# Revit family: HydroTap_Mixer_Zip_Arc
name_source: partatom
category: Plumbing Fixtures
revit_build: Autodesk Revit 2018 (Build: 20190510_1515(x64)
units: mm (PartAtom-declared; Revit-internal decimal feet)

## family parameters
Always vertical = No
Cut with Voids When Loaded = Yes
OmniClass Number = 23.45.55.17
OmniClass Title = Mixing Faucets
Part Type = Normal
Room Calculation Point = No
Round Connector Dimension = Use Diameter
Shared = No
Work Plane-Based = Yes

## types (9) — shared parameters
CW Connection = Yes
HW Connection = Yes
IfcExportAs = IfcValve
IfcExportType = FAUCET
Manufacturer = Zip Australia
ManufacturerOverallDepth = 200 mm
ManufacturerOverallHeight = 353 mm
ManufacturerOverallWidth = 90 mm
ManufacturerURLProductSpecific = https://www.zipwater.com
ModifiedIssue = 20210225 $
URL = https://www.zipwater.com
Uniclass2015Code = Pr_40_20_87_55
Uniclass2015Title = Mixer taps
Uniclass2015Version = Products v1.17
Vent Connection = No
Waste Connection = No
zero-valued in all types: Default Elevation

## per-type parameters (varying)
| type | FixtureMaterial | ManufacturerSpecCode | Model | Type Comments |
| Matte White (Z14) | Metal_MatteWhite_Zip | Z14 | Z14 | Matte White Finish |
| Brushed Stainless Steel (Z13) | Metal_BrushedStainlessSteel_Zip | Z13 | Z13 | Brushed Stainless Steel Finish |
| Brushed Chrome (Z1) | Metal_BrushedChrome_Zip | Z01 | Z1 | Brushed Chrome Finish |
| Brushed Nickel (Z11) | Metal_BrushedNickel_Zip | Z11 | Z11 | Brushed Nickel Finish |
| Brushed Rose Gold (Z5) | Metal_BrushedRoseGold_Zip | Z05 | Z5 | Brushed Rose Gold Finish |
| Brushed Gold (Z7) | Metal_BrushedGold_Zip | Z07 | Z7 | Brushed Gold Finish |
| Chrome (Z0) | Metal_Chrome_Zip | Z00 | Z0 | Chrome Finish |
| Gunmetal (Z9) | Metal_Gunmetal_Zip | Z09 | Z9 | Gunmetal Finish |
| Matte Black (Z3) | Metal_MatteBlack_Zip | Z03 | Z3 | Matte Black Finish |

## geometry (parser evidence)
native form markers: Sweep x3
no freeform markers — native parametric forms only
